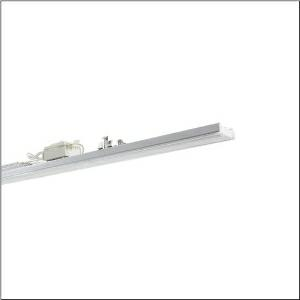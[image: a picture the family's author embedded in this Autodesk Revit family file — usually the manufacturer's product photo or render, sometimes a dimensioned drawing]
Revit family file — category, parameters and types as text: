
# Revit family: licross_21_recessed_ho_52te11dv4l2s
name_source: partatom
category: Lighting Fixtures
units: mm (PartAtom-declared; Revit-internal decimal feet)

## family parameters
Cut with Voids When Loaded = No
Host = Face
Light Source = No
Part Type = Normal
Room Calculation Point = No
Round Connector Dimension = Use Diameter
Shared = No

## types (1)
- --- (1 x LED, 22660 lm, 125.6 W, 4000K)
    Apparent Load = 126 VA
    CIE Flux Codes = 87 95 99 100 100
    Color Rendering = 80
    Color Temperature = 4000K
    Default Elevation = 1800 mm
    Description = Licross 21 Recessed HO, luminaire insert, of sheet steel, galvanised, coil coated, white, length: 2.250mm, width: 66mm, height: 67mm, LED rated luminous flux: 22.660lm, light colour: 840, SDCM (Standard Deviation of Colour Matching)MacAdam ≤ 3 SDCM (initial), control gear: DALI 2, with plug, 5-pole, with phase selection, mains connection: 220..240V, AC, 50/60Hz, rated input power: 126W, internal wiring halogen-free, primary light control with lens, of plastic, primary optical cover: cover, of PMMA, light emission: direct distribution, primary light characteristic: symmetric, protection rating (complete): IP54, insulation class (complete): insulation class I (protective earthing), certification: CE, ENEC, VDE, UKCA, protection symbol: D if used in an environment with non-conductive dust loads with corresponding accessories, impact resistance: IK06, permissible ambient temperature for indoor applications: -40..+30°C, corresponds to IFS (International Featured Standards) requirements for safety and quality in the food industry, reducing of maximum allowable ambient temperature of 5°C with ceiling mounting, LABS conformity tested according to VDMA 24364:2018-05, The light source and the operating device comply with the requirements of the Ecodesign Regulation (EU) 2019/2020 and are replaceable in accordance with this regulation, packaging unit: 1 piece
    Height = 58 mm
    Lamp = 1 x LED
    Lamp Light Flux = 22660 lm
    Lamp Power = 125.6 W
    Lamp count = 1
    Length = 2250 mm
    Luminous efficacy = 180 lm/W
    Manufacturer = Siteco
    ModVariant = No
    Model = 52TE11DV4L2S
    Mounting Place = Ceiling
    Mounting Type = Pendant
    Number of Poles = 1
    OnlyDefault = Yes
    Power Factor = 1
    Product Name = Licross 21 Recessed HO
    Product group = luminaire insert | ceiling pendant
    ProductGroupID = 901
    Protection Class = Protection class I
    Protection Degree = IP 54
    RLX_Detail_Level = 1
    RLX_Emergency_Light_Flux = 0 lm
    RLX_Emergency_Type = 0
    RLX_Emergency_Type_DB = No
    RlxData = <blob elided: 29873 chars, md5=175373dd>
    Socket = socket
    Standby Power = 0 W
    System Light Flux = 22659 lm
    System Power = 126 W
    Type Comments = factory setting: luminous flux: 100 % | dim-lin: 254 | 489 mA
    Type Image = l_1296930.jpg
    URL = http://relux.com
    VarID = @adj_127545
    Voltage = 0 V
    Weight = 0.00 kg
    Width = 66 mm

## geometry (parser evidence)
native form markers: Blend x4, Sweep x10
no freeform markers — native parametric forms only
